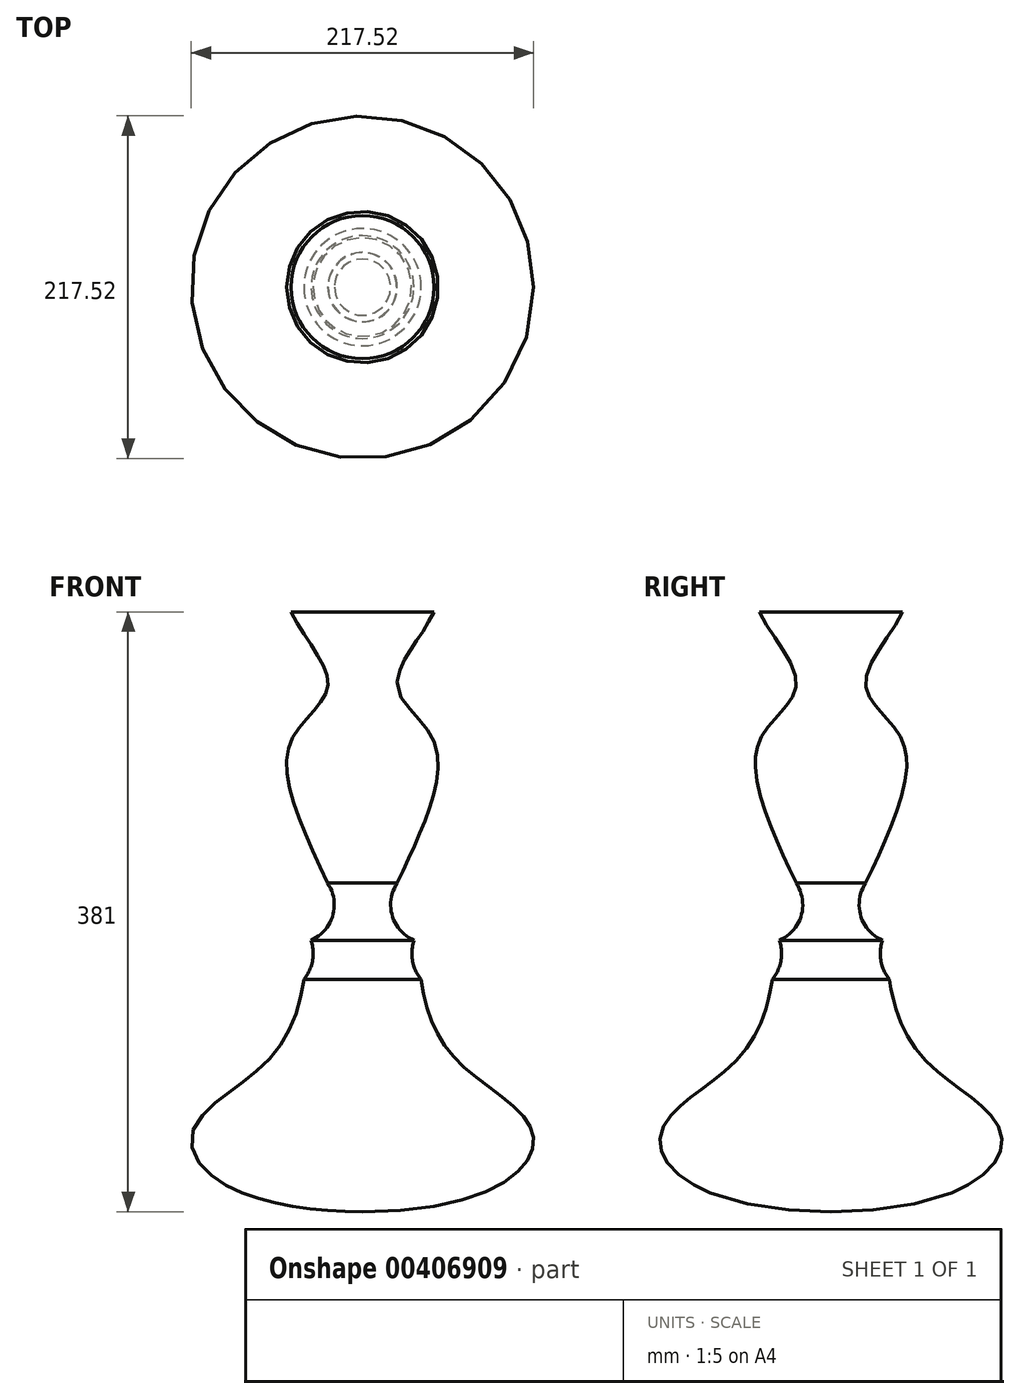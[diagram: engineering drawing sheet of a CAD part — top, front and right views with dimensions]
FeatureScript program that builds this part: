
annotation { "Feature Type Name" : "Feature", "Feature Type Description" : "" }
export const myFeature = defineFeature(function(context is Context, id is Id, definition is map)
    precondition{}
    {
        {
            var Q0;
            Q0=qCreatedBy(makeId("Front.planeOp"),FACE);
            var sketch = newSketch(context, id + "F0", { "sketchPlane" : qUnion([Q0])});
            skLineSegment(sketch, "E0", {"start": v(0, 0) * mm, "end": v(0, 381) * mm});
            skFitSpline(sketch, "E1", {"points": [v(0, 0) * mm, v(108, 50.35) * mm, v(62.05, 94.11) * mm, v(37.2, 147.44) * mm], "startDerivative": vector(594.73, 0) * mm, "endDerivative": vector(-32.34, 215.7) * mm});
            skArc(sketch, "E2", {"start": v(32.66, 172.41) * mm, "mid": v(31.77, 159.35) * mm, "end": v(37.2, 147.44) * mm});
            skArc(sketch, "E3", {"start": v(22.06, 208.66) * mm, "mid": v(18.9, 188.06) * mm, "end": v(32.66, 172.41) * mm});
            skFitSpline(sketch, "E4", {"points": [v(22.06, 208.66) * mm, v(46.18, 296.86) * mm, v(22.06, 333.8) * mm, v(45.43, 381) * mm], "startDerivative": vector(110.86, 239.11) * mm, "endDerivative": vector(75.27, 159.73) * mm});
            skLineSegment(sketch, "E5", {"start": v(0, 381) * mm, "end": v(45.43, 381) * mm});
            skSolve(sketch);
        }
        {
            var Q0;
            Q0=makeQuery(id+"F0.imprint","IMPRINT",FACE,{"disambiguationData":[TD([[makeQuery(id+"F0.imprint","IMPRINT",EDGE,{"derivedFrom":sQuery(id+"F0.wireOp",EDGE,"E0")}),-1.0]])]});
            var Q1;
            Q1=sQuery(id+"F0.wireOp",EDGE,"E0");
            revolve(context, id + "F1", {"entities" : qUnion([Q0]), "axis" : qUnion([Q1]), "revolveType" : RevolveType.FULL});
        }
    });
